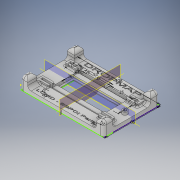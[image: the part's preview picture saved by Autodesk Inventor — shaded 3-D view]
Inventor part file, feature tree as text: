
AUTODESK INVENTOR PART (.ipt)
format: ipt  version: 2019 (Build 230136000, 136)  size: 1,058,816 bytes
history: native  units: mm
features: extrude x15, other x12, sketch x10, move_body x10, direct_edit x5, plane x3, mirror x3, fillet x2
ambient origin geometry x8: Origin, YZ Plane, XZ Plane, XY Plane, X Axis, Y Axis, Z Axis, Center Point
bodies: Solide1 (feature_tree)
feature tree (60):
  sketch  "Esquisse1"
  extrude  "Extrusion1"  Depth=86.0mm
  extrude  "Extrusion2"  Depth=26.0mm
  extrude  "Extrusion3"  Depth=3.2mm
  extrude  "Extrusion4"  Depth=23.0mm
  other  "Modification directe1"
  extrude  "Extrusion5"  Depth=2.0mm TaperAngle=0.0deg
  extrude  "Extrusion6"  Depth=2.0mm TaperAngle=0.0deg
  extrude  "Extrusion7"  Depth=2.0mm TaperAngle=0.0deg
  other  "Modification directe2"
  extrude  "Extrusion8"  Depth=2.0mm TaperAngle=0.0deg
  other  "Modification directe3"
  extrude  "Extrusion9"  Depth=2.0mm TaperAngle=0.0deg
  other  "Modification directe5"
  sketch  "Esquisse11"
  extrude  "Extrusion22"  Depth=2.0mm TaperAngle=0.0deg
  direct_edit  "Direct Edit13"
  extrude  "Extrusion23"  Depth=2.0mm TaperAngle=0.0deg
  direct_edit  "Direct Edit15"
  plane  "Work Plane3"
  mirror  "Mirror3"
  fillet  "Fillet10"  [1 undecoded]
  plane  "Work Plane5"
  extrude  "Extrusion25"  Depth=4.0mm TaperAngle=0.0deg
  direct_edit  "Direct Edit16"
  direct_edit  "Direct Edit17"
  extrude  "Extrusion26"  TaperAngle=0.0deg  [1 undecoded]
  extrude  "Extrusion27"  Depth=2.0mm
  direct_edit  "Direct Edit18"
  extrude  "Extrusion28"  Depth=2.0mm
  fillet  "Fillet11"  Radius=27.0mm
  mirror  "Mirror5"
  mirror  "Mirror6"
  sketch  "Esquisse2"
  sketch  "Esquisse3"
  sketch  "Sketch17"  dims[d0=128.0mm d1=86.0mm]
  sketch  "Sketch18"  dims[d2=38.0mm d3=26.0mm]
  other  "Work Axis2"
  plane  "Work Plane4"
  other  "Work Axis3"
  sketch  "Sketch21"  dims[d4=53.0mm d5=3.2mm]
  sketch  "Sketch22"  dims[d6=35.0mm d7=23.0mm]
  sketch  "Sketch23"  dims[d8=20.0mm d9=0.0mm d10=2.0mm d11=0.0mm]
  sketch  "Sketch24"  dims[d12=1.0mm d13=0.0mm d14=1.0mm d15=0.0mm d16=0.0mm d17=0.0mm d18=53.0mm d19=0.0mm d20=0.0mm d21=53.0mm d22=2.0mm d23=0.0mm d24=6.0mm d25=0.0mm d26=6.0mm d27=0.0mm d31=0.0mm d32=0.0mm d33=-0.25mm d37=4.0mm d38=0.0mm d39=0.0mm d40=0.0mm d41=-0.75mm d45=1.0mm d46=13.5mm d47=27.0mm d48=1.0mm d49=0.0mm d62=0.0mm d63=0.0mm d64=0.45mm d65=0.0mm d66=0.0mm d67=0.45mm d137=5.0mm d138=5.0mm d139=5.0mm d140=5.0mm d141=5.0mm d142=5.0mm d143=5.0mm d144=5.0mm d160=2.0mm d161=0.0mm d162=0.0mm d163=12.0mm d164=0.0mm d165=0.0mm d166=0.0mm d167=-4.0mm d168=0.0mm d169=0.0mm d170=-7.0mm d174=2.0mm d175=0.0mm d179=0.0mm d180=0.0mm d181=-11.0mm d182=0.0mm d183=0.0mm d184=11.0mm d185=0.0mm d186=0.0mm d187=11.0mm d188=90.0deg d189=5.0mm d194=90.0deg d196=10.0mm d197=5.0mm d198=10.0mm d199=0.0mm d200=0.0mm d201=0.0mm d202=-5.0mm d203=0.0mm d204=0.0mm d205=-5.0mm d206=0.0mm d207=0.0mm d208=2.0mm d209=3.0mm d210=3.0mm d211=1.0mm d212=0.0mm d213=8.0mm d214=4.0mm d215=0.0mm d216=0.0mm d217=0.0mm d218=0.75mm d219=3.0mm d220=4.0mm d221=0.0mm d222=2.0mm]
  other  "Déplacer1"
  other  "Déplacer2"
  other  "Déplacer3"
  other  "Déplacer5"
  other  "Déplacer8"
  other  "Déplacer9"
  move_body  "Move23"
  move_body  "Move24"
  move_body  "Move25"
  move_body  "Move28"
  move_body  "Move29"
  move_body  "Move30"
  move_body  "Move31"
  move_body  "Move32"
  move_body  "Move33"
  move_body  "Move34"
note: 2 required parameter values undecoded (feature->parameter linkage not recoverable at this tier; creation-order binding heuristic only, values carry confidence <= 0.55)
